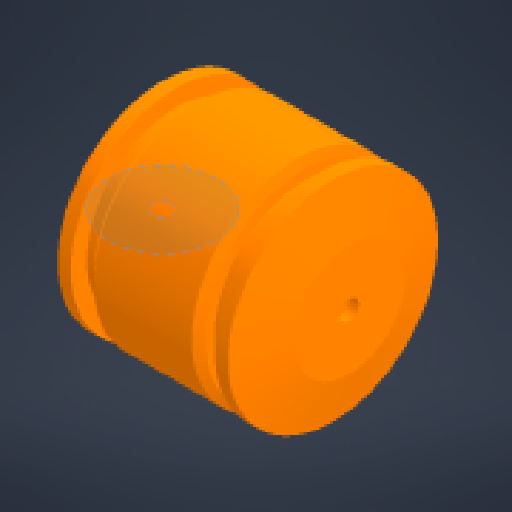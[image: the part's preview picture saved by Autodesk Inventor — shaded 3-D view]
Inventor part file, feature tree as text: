
AUTODESK INVENTOR PART (.ipt)
format: ipt  version: 2024 (Build 280153000, 153)  size: 290,304 bytes
history: native  units: mm
features: reference x6, other x5, sketch x5, extrude x3, revolve x2, shell x1, chamfer x1, projected_geometry x1
ambient origin geometry x8: Origin, YZ Plane, XZ Plane, XY Plane, X Axis, Y Axis, Z Axis, Center Point
bodies: Body1 (feature_tree)
feature tree (24):
  other  "Твердое тело1"
  revolve  "Вращение1"
  revolve  "Вращение2"
  shell  "Оболочка1"  Thickness=32.0mm
  other  "РабПлоскость1"
  chamfer  "Фаска1"  Distance=27.0mm
  extrude  "Выдавливание6"  Depth=5.0mm
  extrude  "Выдавливание17"  Depth=34.0mm
  extrude  "Выдавливание18"  Depth=4.0mm
  sketch  "Эскиз1"
  sketch  "Эскиз2"
  sketch  "Эскиз9"
  sketch  "Эскиз21"
  projected_geometry  "Спроецированная петля5"
  sketch  "Эскиз22"
  reference  "Ссылка19"
  reference  "Ссылка20"
  reference  "Ссылка21"
  reference  "Ссылка22"
  reference  "Ссылка23"
  reference  "Ссылка24"
  parser-record x1  (decoder bookkeeping rows leaked as tree rows — omitted from the tree; the rows remain in map.json)
  other  "wheel_assembly.iam"
  other  "hex:1"
note: 1 file-system path scrubbed to <path> (originals preserved in map.json)
